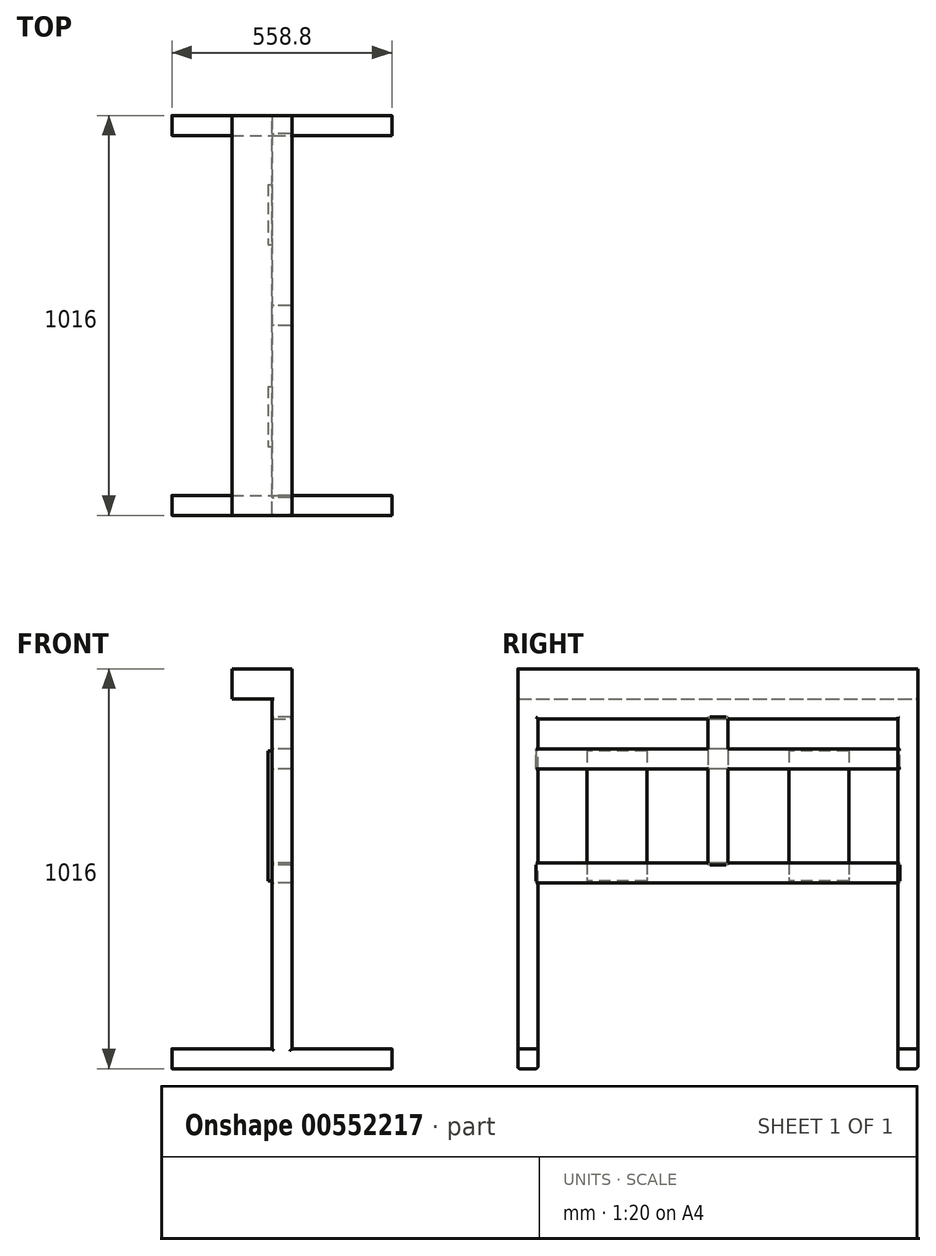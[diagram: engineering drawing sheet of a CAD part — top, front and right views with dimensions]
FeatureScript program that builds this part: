
annotation { "Feature Type Name" : "Feature", "Feature Type Description" : "" }
export const myFeature = defineFeature(function(context is Context, id is Id, definition is map)
    precondition{}
    {
        {
            var Q0;
            Q0=qCreatedBy(makeId("Top.planeOp"),FACE);
            var sketch = newSketch(context, id + "F0", { "sketchPlane" : qUnion([Q0])});
            skLineSegment(sketch, "E0.bottom", {"start": v(152.4, -508) * mm, "end": v(0, -508) * mm});
            skLineSegment(sketch, "E0.top", {"start": v(152.4, 508) * mm, "end": v(0, 508) * mm});
            skLineSegment(sketch, "E0.left", {"start": v(152.4, -508) * mm, "end": v(152.4, 508) * mm});
            skLineSegment(sketch, "E0.right", {"start": v(0, -508) * mm, "end": v(0, 508) * mm});
            skSolve(sketch);
        }
        {
            var Q0;
            Q0=makeQuery(id+"F0.imprint","IMPRINT",FACE,{"disambiguationData":[TD([[makeQuery(id+"F0.imprint","IMPRINT",EDGE,{"derivedFrom":sQuery(id+"F0.wireOp",EDGE,"E0.bottom")}),-1.0]])]});
            extrude(context, id + "F1", {"entities" : qUnion([Q0]), "depth" : 76.2 * mm, "offsetDistance" : 25.4 * mm});
        }
        {
            var Q0;
            Q0=makeQuery(id+"F1.opExtrude","CAP_FACE",FACE,{"disambiguationData":[OSD([sQuery(id+"F0.wireOp",EDGE,"E0.bottom"),sQuery(id+"F0.wireOp",EDGE,"E0.top"),sQuery(id+"F0.wireOp",EDGE,"E0.left"),sQuery(id+"F0.wireOp",EDGE,"E0.right")])],"isStart":true});
            var sketch = newSketch(context, id + "F2", { "sketchPlane" : qUnion([Q0])});
            skLineSegment(sketch, "E1.bottom", {"start": v(152.4, 508) * mm, "end": v(101.6, 508) * mm});
            skLineSegment(sketch, "E1.top", {"start": v(152.4, 457.2) * mm, "end": v(101.6, 457.2) * mm});
            skLineSegment(sketch, "E1.left", {"start": v(152.4, 508) * mm, "end": v(152.4, 457.2) * mm});
            skLineSegment(sketch, "E1.right", {"start": v(101.6, 508) * mm, "end": v(101.6, 457.2) * mm});
            skSolve(sketch);
        }
        {
            var Q0;
            {var subQ4=sQuery(id+"F2.wireOp",EDGE,"E1.top");Q0=makeQuery(id+"F2.imprint","IMPRINT",FACE,{"disambiguationData":[TD([[makeQuery(id+"F2.imprint","IMPRINT",EDGE,{"derivedFrom":subQ4}),1.0]])]});}
            var sketch = newSketch(context, id + "F3", { "sketchPlane" : qUnion([Q0])});
            skLineSegment(sketch, "E2.bottom", {"start": v(152.4, -508) * mm, "end": v(101.6, -508) * mm});
            skLineSegment(sketch, "E2.top", {"start": v(152.4, -457.2) * mm, "end": v(101.6, -457.2) * mm});
            skLineSegment(sketch, "E2.left", {"start": v(152.4, -508) * mm, "end": v(152.4, -457.2) * mm});
            skLineSegment(sketch, "E2.right", {"start": v(101.6, -508) * mm, "end": v(101.6, -457.2) * mm});
            skSolve(sketch);
        }
        {
            var Q0;
            {var subQ4=sQuery(id+"F2.wireOp",EDGE,"E1.top");Q0=makeQuery(id+"F2.imprint","IMPRINT",FACE,{"disambiguationData":[TD([[makeQuery(id+"F2.imprint","IMPRINT",EDGE,{"derivedFrom":subQ4}),1.0]])]});}
            var sketch = newSketch(context, id + "F4", { "sketchPlane" : qUnion([Q0])});
            skLineSegment(sketch, "E3.bottom", {"start": v(101.6, 457.2) * mm, "end": v(152.4, 457.2) * mm});
            skLineSegment(sketch, "E3.top", {"start": v(101.6, -457.2) * mm, "end": v(152.4, -457.2) * mm});
            skLineSegment(sketch, "E3.left", {"start": v(101.6, 457.2) * mm, "end": v(101.6, -457.2) * mm});
            skLineSegment(sketch, "E3.right", {"start": v(152.4, 457.2) * mm, "end": v(152.4, -457.2) * mm});
            skSolve(sketch);
        }
        {
            var Q0;
            Q0 = qSketchRegion(id + "F4", true);
            extrude(context, id + "F5", {"entities" : qUnion([Q0]), "operationType" : NewBodyOperationType.ADD, "depth" : 50.8 * mm, "offsetDistance" : 25.4 * mm});
        }
        {
            var Q0;
            Q0=makeQuery(id+"F5.opExtrude","CAP_EDGE",EDGE,{"disambiguationData":[OSD([sQuery(id+"F4.wireOp",EDGE,"E3.left")])],"isStart":false});
            var Q1;
            Q1=makeQuery(id+"F5.opExtrude","CAP_EDGE",EDGE,{"disambiguationData":[OSD([sQuery(id+"F4.wireOp",EDGE,"E3.right")])],"isStart":false});
            fillet(context, id + "F6", {"entities" : qUnion([Q0, Q1]), "radius" : 5.08 * mm, "tangentPropagation" : true, "allowEdgeOverflow" : false});
        }
        {
            var Q0;
            Q0=makeQuery(id+"F2.imprint","IMPRINT",FACE,{"disambiguationData":[TD([[makeQuery(id+"F2.imprint","IMPRINT",EDGE,{"derivedFrom":sQuery(id+"F2.wireOp",EDGE,"E1.bottom")}),1.0]])]});
            extrude(context, id + "F7", {"entities" : qUnion([Q0]), "operationType" : NewBodyOperationType.ADD, "depth" : 889 * mm, "offsetDistance" : 25.4 * mm});
        }
        {
            var Q0;
            Q0=makeQuery(id+"F3.imprint","IMPRINT",FACE,{"disambiguationData":[TD([[makeQuery(id+"F3.imprint","IMPRINT",EDGE,{"derivedFrom":sQuery(id+"F3.wireOp",EDGE,"E2.bottom")}),-1.0]])]});
            extrude(context, id + "F8", {"entities" : qUnion([Q0]), "operationType" : NewBodyOperationType.ADD, "depth" : 889 * mm, "offsetDistance" : 25.4 * mm});
        }
        {
            var Q0;
            Q0=makeQuery(id+"F7.opExtrude","SWEPT_EDGE",EDGE,{"disambiguationData":[OSD([sQuery(id+"F2.wireOp",EDGE,"E1.top"),sQuery(id+"F2.wireOp",EDGE,"E1.right")])]});
            var Q1;
            Q1=makeQuery(id+"F7.opExtrude","SWEPT_EDGE",EDGE,{"disambiguationData":[OSD([sQuery(id+"F0.wireOp",EDGE,"E0.left"),sQuery(id+"F2.wireOp",EDGE,"E1.top"),sQuery(id+"F2.wireOp",EDGE,"E1.left")])]});
            var Q2;
            Q2=makeQuery(id+"F7.opExtrude","SWEPT_EDGE",EDGE,{"disambiguationData":[OSD([sQuery(id+"F0.wireOp",EDGE,"E0.bottom"),sQuery(id+"F2.wireOp",EDGE,"E1.bottom"),sQuery(id+"F2.wireOp",EDGE,"E1.right")])]});
            var Q3;
            Q3=makeQuery(id+"F7.boolean.opBoolean","MERGE",EDGE,{"derivedFrom":[makeQuery(id+"F1.opExtrude","SWEPT_EDGE",EDGE,{"disambiguationData":[OSD([sQuery(id+"F0.wireOp",EDGE,"E0.bottom"),sQuery(id+"F0.wireOp",EDGE,"E0.left")])]}),makeQuery(id+"F7.opExtrude","SWEPT_EDGE",EDGE,{"disambiguationData":[OSD([sQuery(id+"F2.wireOp",EDGE,"E1.bottom"),sQuery(id+"F2.wireOp",EDGE,"E1.left")])]})]});
            var Q4;
            Q4=makeQuery(id+"F8.boolean.opBoolean","MERGE",EDGE,{"derivedFrom":[makeQuery(id+"F1.opExtrude","SWEPT_EDGE",EDGE,{"disambiguationData":[OSD([sQuery(id+"F0.wireOp",EDGE,"E0.top"),sQuery(id+"F0.wireOp",EDGE,"E0.left")])]}),makeQuery(id+"F8.opExtrude","SWEPT_EDGE",EDGE,{"disambiguationData":[OSD([sQuery(id+"F3.wireOp",EDGE,"E2.bottom"),sQuery(id+"F3.wireOp",EDGE,"E2.left")])]})]});
            var Q5;
            Q5=makeQuery(id+"F8.opExtrude","SWEPT_EDGE",EDGE,{"disambiguationData":[OSD([sQuery(id+"F0.wireOp",EDGE,"E0.top"),sQuery(id+"F3.wireOp",EDGE,"E2.bottom"),sQuery(id+"F3.wireOp",EDGE,"E2.right")])]});
            var Q6;
            Q6=makeQuery(id+"F8.opExtrude","SWEPT_EDGE",EDGE,{"disambiguationData":[OSD([sQuery(id+"F3.wireOp",EDGE,"E2.top"),sQuery(id+"F3.wireOp",EDGE,"E2.right")])]});
            fillet(context, id + "F9", {"entities" : qUnion([Q0, Q1, Q2, Q3, Q4, Q5, Q6]), "radius" : 5.08 * mm, "tangentPropagation" : true, "allowEdgeOverflow" : false});
        }
        {
            var Q0;
            Q0=makeQuery(id+"F8.boolean.opBoolean","MERGE",FACE,{"derivedFrom":[makeQuery(id+"F7.boolean.opBoolean","MERGE",FACE,{"derivedFrom":[makeQuery(id+"F5.opExtrude","SWEPT_FACE",FACE,{"disambiguationData":[OSD([sQuery(id+"F4.wireOp",EDGE,"E3.left")])]}),makeQuery(id+"F7.opExtrude","SWEPT_FACE",FACE,{"disambiguationData":[OSD([sQuery(id+"F2.wireOp",EDGE,"E1.right")])]})]}),makeQuery(id+"F8.opExtrude","SWEPT_FACE",FACE,{"disambiguationData":[OSD([sQuery(id+"F3.wireOp",EDGE,"E2.right")])]})]});
            var sketch = newSketch(context, id + "F10", { "sketchPlane" : qUnion([Q0])});
            skLineSegment(sketch, "E4.bottom", {"start": v(-462.28, -127) * mm, "end": v(462.28, -127) * mm});
            skLineSegment(sketch, "E4.top", {"start": v(-462.28, -177.8) * mm, "end": v(462.28, -177.8) * mm});
            skLineSegment(sketch, "E4.left", {"start": v(-462.28, -127) * mm, "end": v(-462.28, -177.8) * mm});
            skLineSegment(sketch, "E4.right", {"start": v(462.28, -127) * mm, "end": v(462.28, -177.8) * mm});
            skSolve(sketch);
        }
        {
            var Q0;
            Q0=makeQuery(id+"F10.imprint","IMPRINT",FACE,{"disambiguationData":[TD([[makeQuery(id+"F10.imprint","IMPRINT",EDGE,{"derivedFrom":sQuery(id+"F10.wireOp",EDGE,"E4.bottom")}),-1.0]])]});
            extrude(context, id + "F11", {"entities" : qUnion([Q0]), "oppositeDirection" : true, "depth" : 50.8 * mm, "offsetDistance" : 25.4 * mm});
        }
        {
            var Q0;
            Q0=makeQuery(id+"F11.opExtrude","CAP_EDGE",EDGE,{"disambiguationData":[OSD([sQuery(id+"F10.wireOp",EDGE,"E4.bottom")])],"isStart":true});
            var Q1;
            Q1=makeQuery(id+"F11.opExtrude","CAP_EDGE",EDGE,{"disambiguationData":[OSD([sQuery(id+"F10.wireOp",EDGE,"E4.top")])],"isStart":true});
            var Q2;
            Q2=makeQuery(id+"F11.opExtrude","CAP_FACE",FACE,{"disambiguationData":[OSD([sQuery(id+"F10.wireOp",EDGE,"E4.bottom"),sQuery(id+"F10.wireOp",EDGE,"E4.top"),sQuery(id+"F10.wireOp",EDGE,"E4.left"),sQuery(id+"F10.wireOp",EDGE,"E4.right")])],"isStart":false});
            var Q3;
            Q3=makeQuery(id+"F11.opExtrude","CAP_EDGE",EDGE,{"disambiguationData":[OSD([sQuery(id+"F10.wireOp",EDGE,"E4.top")])],"isStart":false});
            fillet(context, id + "F12", {"entities" : qUnion([Q0, Q1, Q2, Q3]), "radius" : 5.08 * mm, "tangentPropagation" : true, "allowEdgeOverflow" : false});
        }
        {
            var Q0;
            Q0=makeQuery(id+"F8.boolean.opBoolean","MERGE",FACE,{"derivedFrom":[makeQuery(id+"F7.boolean.opBoolean","MERGE",FACE,{"derivedFrom":[makeQuery(id+"F5.opExtrude","SWEPT_FACE",FACE,{"disambiguationData":[OSD([sQuery(id+"F4.wireOp",EDGE,"E3.left")])]}),makeQuery(id+"F7.opExtrude","SWEPT_FACE",FACE,{"disambiguationData":[OSD([sQuery(id+"F2.wireOp",EDGE,"E1.right")])]})]}),makeQuery(id+"F8.opExtrude","SWEPT_FACE",FACE,{"disambiguationData":[OSD([sQuery(id+"F3.wireOp",EDGE,"E2.right")])]})]});
            var sketch = newSketch(context, id + "F13", { "sketchPlane" : qUnion([Q0])});
            skLineSegment(sketch, "E5.bottom", {"start": v(-462.28, -416.56) * mm, "end": v(462.28, -416.56) * mm});
            skLineSegment(sketch, "E5.top", {"start": v(-462.28, -467.36) * mm, "end": v(462.28, -467.36) * mm});
            skLineSegment(sketch, "E5.left", {"start": v(-462.28, -416.56) * mm, "end": v(-462.28, -467.36) * mm});
            skLineSegment(sketch, "E5.right", {"start": v(462.28, -416.56) * mm, "end": v(462.28, -467.36) * mm});
            skSolve(sketch);
        }
        {
            var Q0;
            Q0=makeQuery(id+"F13.imprint","IMPRINT",FACE,{"disambiguationData":[TD([[makeQuery(id+"F13.imprint","IMPRINT",EDGE,{"derivedFrom":sQuery(id+"F13.wireOp",EDGE,"E5.bottom")}),-1.0]])]});
            extrude(context, id + "F14", {"entities" : qUnion([Q0]), "oppositeDirection" : true, "depth" : 50.8 * mm, "offsetDistance" : 25.4 * mm});
        }
        {
            var Q0;
            Q0=makeQuery(id+"F14.opExtrude","CAP_EDGE",EDGE,{"disambiguationData":[OSD([sQuery(id+"F13.wireOp",EDGE,"E5.bottom")])],"isStart":true});
            var Q1;
            Q1=makeQuery(id+"F14.opExtrude","CAP_EDGE",EDGE,{"disambiguationData":[OSD([sQuery(id+"F13.wireOp",EDGE,"E5.top")])],"isStart":true});
            var Q2;
            Q2=makeQuery(id+"F14.opExtrude","CAP_EDGE",EDGE,{"disambiguationData":[OSD([sQuery(id+"F13.wireOp",EDGE,"E5.top")])],"isStart":false});
            var Q3;
            Q3=makeQuery(id+"F14.opExtrude","CAP_EDGE",EDGE,{"disambiguationData":[OSD([sQuery(id+"F13.wireOp",EDGE,"E5.bottom")])],"isStart":false});
            fillet(context, id + "F15", {"entities" : qUnion([Q0, Q1, Q2, Q3]), "radius" : 5.08 * mm, "tangentPropagation" : true, "allowEdgeOverflow" : false});
        }
        {
            var Q0;
            Q0=makeQuery(id+"F8.boolean.opBoolean","MERGE",FACE,{"derivedFrom":[makeQuery(id+"F7.boolean.opBoolean","MERGE",FACE,{"derivedFrom":[makeQuery(id+"F5.opExtrude","SWEPT_FACE",FACE,{"disambiguationData":[OSD([sQuery(id+"F4.wireOp",EDGE,"E3.left")])]}),makeQuery(id+"F7.opExtrude","SWEPT_FACE",FACE,{"disambiguationData":[OSD([sQuery(id+"F2.wireOp",EDGE,"E1.right")])]})]}),makeQuery(id+"F8.opExtrude","SWEPT_FACE",FACE,{"disambiguationData":[OSD([sQuery(id+"F3.wireOp",EDGE,"E2.right")])]})]});
            var sketch = newSketch(context, id + "F16", { "sketchPlane" : qUnion([Q0])});
            skLineSegment(sketch, "E6.bottom", {"start": v(-25.4, -45.72) * mm, "end": v(25.4, -45.72) * mm});
            skLineSegment(sketch, "E6.top", {"start": v(-25.4, -421.64) * mm, "end": v(25.4, -421.64) * mm});
            skLineSegment(sketch, "E6.left", {"start": v(-25.4, -45.72) * mm, "end": v(-25.4, -421.64) * mm});
            skLineSegment(sketch, "E6.right", {"start": v(25.4, -45.72) * mm, "end": v(25.4, -421.64) * mm});
            skSolve(sketch);
        }
        {
            var Q0;
            Q0=makeQuery(id+"F16.imprint","IMPRINT",FACE,{"disambiguationData":[TD([[makeQuery(id+"F16.imprint","IMPRINT",EDGE,{"derivedFrom":sQuery(id+"F16.wireOp",EDGE,"E6.bottom")}),-1.0]])]});
            extrude(context, id + "F17", {"entities" : qUnion([Q0]), "oppositeDirection" : true, "depth" : 50.8 * mm, "offsetDistance" : 25.4 * mm});
        }
        {
            var Q0;
            Q0=makeQuery(id+"F17.opExtrude","CAP_EDGE",EDGE,{"disambiguationData":[OSD([sQuery(id+"F16.wireOp",EDGE,"E6.right")])],"isStart":true});
            var Q1;
            Q1=makeQuery(id+"F17.opExtrude","CAP_EDGE",EDGE,{"disambiguationData":[OSD([sQuery(id+"F16.wireOp",EDGE,"E6.left")])],"isStart":true});
            var Q2;
            Q2=makeQuery(id+"F17.opExtrude","CAP_EDGE",EDGE,{"disambiguationData":[OSD([sQuery(id+"F16.wireOp",EDGE,"E6.right")])],"isStart":false});
            var Q3;
            Q3=makeQuery(id+"F17.opExtrude","CAP_EDGE",EDGE,{"disambiguationData":[OSD([sQuery(id+"F16.wireOp",EDGE,"E6.left")])],"isStart":false});
            fillet(context, id + "F18", {"entities" : qUnion([Q0, Q1, Q2, Q3]), "radius" : 5.08 * mm, "tangentPropagation" : true, "allowEdgeOverflow" : false});
        }
        {
            var Q0;
            Q0=makeQuery(id+"F11.opExtrude","CAP_FACE",FACE,{"disambiguationData":[OSD([sQuery(id+"F10.wireOp",EDGE,"E4.bottom"),sQuery(id+"F10.wireOp",EDGE,"E4.top"),sQuery(id+"F10.wireOp",EDGE,"E4.left"),sQuery(id+"F10.wireOp",EDGE,"E4.right")])],"isStart":true});
            var sketch = newSketch(context, id + "F19", { "sketchPlane" : qUnion([Q0])});
            skLineSegment(sketch, "E7.bottom", {"start": v(-332.74, -132.08) * mm, "end": v(-180.34, -132.08) * mm});
            skLineSegment(sketch, "E7.top", {"start": v(-332.74, -462.28) * mm, "end": v(-180.34, -462.28) * mm});
            skLineSegment(sketch, "E7.left", {"start": v(-332.74, -132.08) * mm, "end": v(-332.74, -462.28) * mm});
            skLineSegment(sketch, "E7.right", {"start": v(-180.34, -132.08) * mm, "end": v(-180.34, -462.28) * mm});
            skSolve(sketch);
        }
        {
            var Q0;
            {var subQ0=sQuery(id+"F19.wireOp",EDGE,"E7.bottom");Q0=makeQuery(id+"F19.imprint","IMPRINT",FACE,{"disambiguationData":[TD([[makeQuery(id+"F19.imprint","IMPRINT",EDGE,{"derivedFrom":subQ0}),1.0]])]});}
            var Q1;
            {var subQ0=sQuery(id+"F19.wireOp",EDGE,"E7.top");Q1=makeQuery(id+"F19.imprint","IMPRINT",FACE,{"disambiguationData":[TD([[makeQuery(id+"F19.imprint","IMPRINT",EDGE,{"derivedFrom":subQ0}),1.0]])]});}
            extrude(context, id + "F20", {"entities" : qUnion([Q0, Q1]), "depth" : 9.52 * mm, "offsetDistance" : 25.4 * mm});
        }
        {
            var Q0;
            Q0=makeQuery(id+"F11.opExtrude","CAP_FACE",FACE,{"disambiguationData":[OSD([sQuery(id+"F10.wireOp",EDGE,"E4.bottom"),sQuery(id+"F10.wireOp",EDGE,"E4.top"),sQuery(id+"F10.wireOp",EDGE,"E4.left"),sQuery(id+"F10.wireOp",EDGE,"E4.right")])],"isStart":true});
            var sketch = newSketch(context, id + "F21", { "sketchPlane" : qUnion([Q0])});
            skLineSegment(sketch, "E8.bottom", {"start": v(180.34, -132.08) * mm, "end": v(332.74, -132.08) * mm});
            skLineSegment(sketch, "E8.top", {"start": v(180.34, -462.28) * mm, "end": v(332.74, -462.28) * mm});
            skLineSegment(sketch, "E8.left", {"start": v(180.34, -132.08) * mm, "end": v(180.34, -462.28) * mm});
            skLineSegment(sketch, "E8.right", {"start": v(332.74, -132.08) * mm, "end": v(332.74, -462.28) * mm});
            skSolve(sketch);
        }
        {
            var Q0;
            {var subQ0=sQuery(id+"F21.wireOp",EDGE,"E8.top");Q0=makeQuery(id+"F21.imprint","IMPRINT",FACE,{"disambiguationData":[TD([[makeQuery(id+"F21.imprint","IMPRINT",EDGE,{"derivedFrom":subQ0}),1.0]])]});}
            var Q1;
            {var subQ0=sQuery(id+"F21.wireOp",EDGE,"E8.bottom");Q1=makeQuery(id+"F21.imprint","IMPRINT",FACE,{"disambiguationData":[TD([[makeQuery(id+"F21.imprint","IMPRINT",EDGE,{"derivedFrom":subQ0}),1.0]])]});}
            extrude(context, id + "F22", {"entities" : qUnion([Q0, Q1]), "depth" : 9.52 * mm, "offsetDistance" : 25.4 * mm});
        }
        {
            var Q0;
            Q0=makeQuery(id+"F7.opExtrude","CAP_FACE",FACE,{"disambiguationData":[OSD([sQuery(id+"F2.wireOp",EDGE,"E1.bottom"),sQuery(id+"F2.wireOp",EDGE,"E1.top"),sQuery(id+"F2.wireOp",EDGE,"E1.left"),sQuery(id+"F2.wireOp",EDGE,"E1.right")])],"isStart":false});
            var sketch = newSketch(context, id + "F23", { "sketchPlane" : qUnion([Q0])});
            skPoint(sketch, "E9.oppositeSnap0", {"position": v(127, 457.2) * mm});
            skLineSegment(sketch, "E9.bottom", {"start": v(-152.4, 508) * mm, "end": v(406.4, 508) * mm});
            skLineSegment(sketch, "E9.top", {"start": v(-152.4, 457.2) * mm, "end": v(406.4, 457.2) * mm});
            skLineSegment(sketch, "E9.left", {"start": v(-152.4, 508) * mm, "end": v(-152.4, 457.2) * mm});
            skLineSegment(sketch, "E9.right", {"start": v(406.4, 508) * mm, "end": v(406.4, 457.2) * mm});
            skSolve(sketch);
        }
        {
            var Q0;
            {var subQ7=sQuery(id+"F23.wireOp",EDGE,"E9.right");Q0=makeQuery(id+"F23.imprint","IMPRINT",FACE,{"disambiguationData":[TD([[makeQuery(id+"F23.imprint","IMPRINT",EDGE,{"derivedFrom":subQ7}),-1.0]])]});}
            var Q1;
            {var subQ0=sQuery(id+"F2.wireOp",EDGE,"E1.left");Q1=makeQuery(id+"F23.imprint","IMPRINT",FACE,{"disambiguationData":[TD([[makeQuery(id+"F23.imprint","IMPRINT",EDGE,{"derivedFrom":makeQuery(id+"F7.opExtrude","CAP_EDGE",EDGE,{"disambiguationData":[OSD([subQ0])],"isStart":false})}),-1.0]])]});}
            var Q2;
            {var subQ7=sQuery(id+"F23.wireOp",EDGE,"E9.left");Q2=makeQuery(id+"F23.imprint","IMPRINT",FACE,{"disambiguationData":[TD([[makeQuery(id+"F23.imprint","IMPRINT",EDGE,{"derivedFrom":subQ7}),1.0]])]});}
            extrude(context, id + "F24", {"entities" : qUnion([Q0, Q1, Q2]), "operationType" : NewBodyOperationType.ADD, "depth" : 50.8 * mm, "offsetDistance" : 25.4 * mm});
        }
        {
            var Q0;
            {var subQ0=sQuery(id+"F23.wireOp",EDGE,"E9.bottom");var subQ3=sQuery(id+"F23.wireOp",EDGE,"E9.left");Q0=makeQuery(id+"F24.boolean.opBoolean","SPLIT",EDGE,{"disambiguationData":[TD([makeQuery(id+"F24.opExtrude","SWEPT_FACE",FACE,{"disambiguationData":[OSD([subQ3])]})])],"derivedFrom":makeQuery(id+"F24.opExtrude","CAP_EDGE",EDGE,{"disambiguationData":[OSD([subQ0])],"isStart":true})});}
            var Q1;
            Q1=makeQuery(id+"F24.opExtrude","CAP_EDGE",EDGE,{"disambiguationData":[OSD([sQuery(id+"F23.wireOp",EDGE,"E9.bottom")])],"isStart":false});
            var Q2;
            {var subQ0=sQuery(id+"F23.wireOp",EDGE,"E9.bottom");var subQ3=sQuery(id+"F23.wireOp",EDGE,"E9.right");Q2=makeQuery(id+"F24.boolean.opBoolean","SPLIT",EDGE,{"disambiguationData":[TD([makeQuery(id+"F24.opExtrude","SWEPT_FACE",FACE,{"disambiguationData":[OSD([subQ3])]})])],"derivedFrom":makeQuery(id+"F24.opExtrude","CAP_EDGE",EDGE,{"disambiguationData":[OSD([subQ0])],"isStart":true})});}
            var Q3;
            {var subQ0=sQuery(id+"F23.wireOp",EDGE,"E9.left");var subQ1=sQuery(id+"F23.wireOp",EDGE,"E9.top");Q3=makeQuery(id+"F24.boolean.opBoolean","SPLIT",EDGE,{"disambiguationData":[TD([makeQuery(id+"F24.opExtrude","SWEPT_FACE",FACE,{"disambiguationData":[OSD([subQ0])]})])],"derivedFrom":makeQuery(id+"F24.opExtrude","CAP_EDGE",EDGE,{"disambiguationData":[OSD([subQ1])],"isStart":true})});}
            var Q4;
            {var subQ0=sQuery(id+"F23.wireOp",EDGE,"E9.top");var subQ1=sQuery(id+"F23.wireOp",EDGE,"E9.right");Q4=makeQuery(id+"F24.boolean.opBoolean","SPLIT",EDGE,{"disambiguationData":[TD([makeQuery(id+"F24.opExtrude","SWEPT_FACE",FACE,{"disambiguationData":[OSD([subQ1])]})])],"derivedFrom":makeQuery(id+"F24.opExtrude","CAP_EDGE",EDGE,{"disambiguationData":[OSD([subQ0])],"isStart":true})});}
            var Q5;
            Q5=makeQuery(id+"F24.opExtrude","CAP_EDGE",EDGE,{"disambiguationData":[OSD([sQuery(id+"F23.wireOp",EDGE,"E9.top")])],"isStart":false});
            fillet(context, id + "F25", {"entities" : qUnion([Q0, Q1, Q2, Q3, Q4, Q5]), "radius" : 5.08 * mm, "tangentPropagation" : true, "allowEdgeOverflow" : false});
        }
        {
            var Q0;
            Q0=makeQuery(id+"F8.opExtrude","CAP_FACE",FACE,{"disambiguationData":[OSD([sQuery(id+"F3.wireOp",EDGE,"E2.bottom"),sQuery(id+"F3.wireOp",EDGE,"E2.top"),sQuery(id+"F3.wireOp",EDGE,"E2.left"),sQuery(id+"F3.wireOp",EDGE,"E2.right")])],"isStart":false});
            var sketch = newSketch(context, id + "F26", { "sketchPlane" : qUnion([Q0])});
            skPoint(sketch, "E10.firstSnap0", {"position": v(129.54, -457.2) * mm});
            skLineSegment(sketch, "E10.bottom", {"start": v(-152.4, -457.2) * mm, "end": v(406.4, -457.2) * mm});
            skLineSegment(sketch, "E10.top", {"start": v(-152.4, -508) * mm, "end": v(406.4, -508) * mm});
            skLineSegment(sketch, "E10.left", {"start": v(-152.4, -457.2) * mm, "end": v(-152.4, -508) * mm});
            skLineSegment(sketch, "E10.right", {"start": v(406.4, -457.2) * mm, "end": v(406.4, -508) * mm});
            skSolve(sketch);
        }
        {
            var Q0;
            {var subQ0=sQuery(id+"F26.wireOp",EDGE,"E10.right");Q0=makeQuery(id+"F26.imprint","IMPRINT",FACE,{"disambiguationData":[TD([[makeQuery(id+"F26.imprint","IMPRINT",EDGE,{"derivedFrom":subQ0}),-1.0]])]});}
            var Q1;
            {var subQ0=sQuery(id+"F3.wireOp",EDGE,"E2.right");Q1=makeQuery(id+"F26.imprint","IMPRINT",FACE,{"disambiguationData":[TD([[makeQuery(id+"F26.imprint","IMPRINT",EDGE,{"derivedFrom":makeQuery(id+"F8.opExtrude","CAP_EDGE",EDGE,{"disambiguationData":[OSD([subQ0])],"isStart":false})}),-1.0]])]});}
            var Q2;
            {var subQ0=sQuery(id+"F26.wireOp",EDGE,"E10.left");Q2=makeQuery(id+"F26.imprint","IMPRINT",FACE,{"disambiguationData":[TD([[makeQuery(id+"F26.imprint","IMPRINT",EDGE,{"derivedFrom":subQ0}),1.0]])]});}
            extrude(context, id + "F27", {"entities" : qUnion([Q0, Q1, Q2]), "operationType" : NewBodyOperationType.ADD, "depth" : 50.8 * mm, "offsetDistance" : 25.4 * mm});
        }
        {
            var Q0;
            Q0=makeQuery(id+"F27.opExtrude","CAP_EDGE",EDGE,{"disambiguationData":[OSD([sQuery(id+"F26.wireOp",EDGE,"E10.bottom")])],"isStart":false});
            var Q1;
            Q1=makeQuery(id+"F27.opExtrude","CAP_EDGE",EDGE,{"disambiguationData":[OSD([sQuery(id+"F26.wireOp",EDGE,"E10.top")])],"isStart":false});
            var Q2;
            {var subQ0=sQuery(id+"F26.wireOp",EDGE,"E10.left");var subQ1=sQuery(id+"F26.wireOp",EDGE,"E10.bottom");Q2=makeQuery(id+"F27.boolean.opBoolean","SPLIT",EDGE,{"disambiguationData":[TD([makeQuery(id+"F27.opExtrude","SWEPT_FACE",FACE,{"disambiguationData":[OSD([subQ0])]})])],"derivedFrom":makeQuery(id+"F27.opExtrude","CAP_EDGE",EDGE,{"disambiguationData":[OSD([subQ1])],"isStart":true})});}
            var Q3;
            {var subQ1=sQuery(id+"F26.wireOp",EDGE,"E10.top");var subQ2=sQuery(id+"F26.wireOp",EDGE,"E10.left");Q3=makeQuery(id+"F27.boolean.opBoolean","SPLIT",EDGE,{"disambiguationData":[TD([makeQuery(id+"F27.opExtrude","SWEPT_FACE",FACE,{"disambiguationData":[OSD([subQ2])]})])],"derivedFrom":makeQuery(id+"F27.opExtrude","CAP_EDGE",EDGE,{"disambiguationData":[OSD([subQ1])],"isStart":true})});}
            var Q4;
            {var subQ0=sQuery(id+"F26.wireOp",EDGE,"E10.bottom");Q4=makeQuery(id+"F27.boolean.opBoolean","SPLIT",EDGE,{"disambiguationData":[TD([makeQuery(id+"F1.opExtrude","SWEPT_FACE",FACE,{"disambiguationData":[OSD([sQuery(id+"F0.wireOp",EDGE,"E0.left")])]})])],"derivedFrom":makeQuery(id+"F27.opExtrude","CAP_EDGE",EDGE,{"disambiguationData":[OSD([subQ0])],"isStart":true})});}
            var Q5;
            {var subQ2=sQuery(id+"F26.wireOp",EDGE,"E10.right");var subQ3=sQuery(id+"F26.wireOp",EDGE,"E10.top");Q5=makeQuery(id+"F27.boolean.opBoolean","SPLIT",EDGE,{"disambiguationData":[TD([makeQuery(id+"F27.opExtrude","SWEPT_FACE",FACE,{"disambiguationData":[OSD([subQ2])]})])],"derivedFrom":makeQuery(id+"F27.opExtrude","CAP_EDGE",EDGE,{"disambiguationData":[OSD([subQ3])],"isStart":true})});}
            fillet(context, id + "F28", {"entities" : qUnion([Q0, Q1, Q2, Q3, Q4, Q5]), "radius" : 5.08 * mm, "tangentPropagation" : true, "allowEdgeOverflow" : false});
        }
    });
